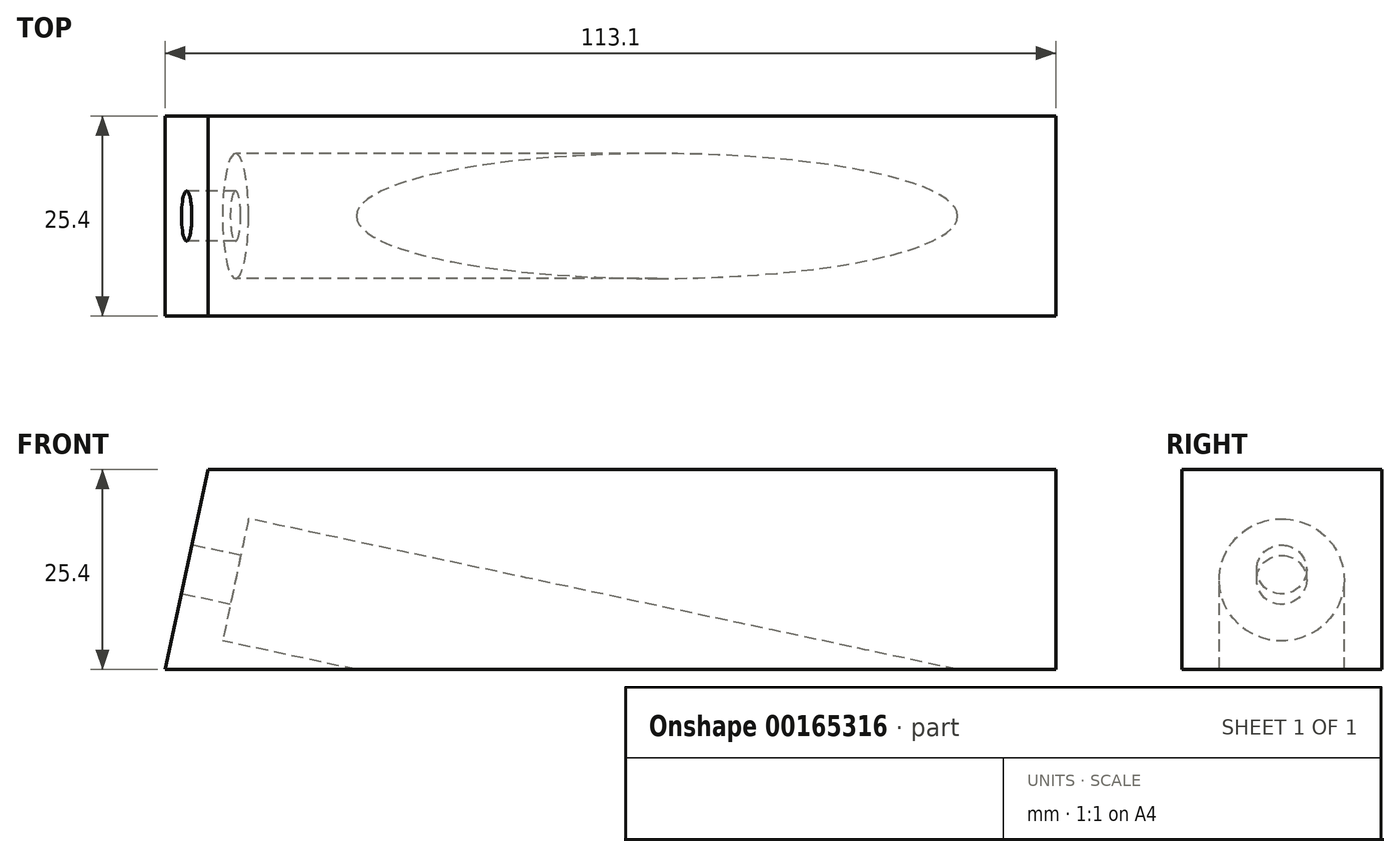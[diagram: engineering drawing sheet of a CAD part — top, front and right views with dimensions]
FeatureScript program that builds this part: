
annotation { "Feature Type Name" : "Feature", "Feature Type Description" : "" }
export const myFeature = defineFeature(function(context is Context, id is Id, definition is map)
    precondition{}
    {
        {
            var Q0;
            Q0=qCreatedBy(makeId("Front.planeOp"),FACE);
            var sketch = newSketch(context, id + "F0", { "sketchPlane" : qUnion([Q0])});
            skLineSegment(sketch, "E0", {"start": v(5.4, 25.4) * mm, "end": v(0, 0) * mm});
            skLineSegment(sketch, "E1", {"start": v(0, 0) * mm, "end": v(113.1, 0) * mm});
            skLineSegment(sketch, "E2", {"start": v(113.1, 0) * mm, "end": v(113.1, 25.4) * mm});
            skLineSegment(sketch, "E3", {"start": v(113.1, 25.4) * mm, "end": v(5.4, 25.4) * mm});
            skSolve(sketch);
        }
        {
            var Q0;
            Q0 = qSketchRegion(id + "F0", true);
            extrude(context, id + "F1", {"entities" : qUnion([Q0]), "endBound" : BoundingType.SYMMETRIC, "depth" : 25.4 * mm});
        }
        {
            var Q0;
            Q0=makeQuery(id+"F1.opExtrude","SWEPT_FACE",FACE,{"disambiguationData":[OSD([sQuery(id+"F0.wireOp",EDGE,"E0")])]});
            var sketch = newSketch(context, id + "F2", { "sketchPlane" : qUnion([Q0])});
            skCircle(sketch, "E4", {"center": v(0, 12.98) * mm, "radius": 3.18 * mm});
            skPoint(sketch, "E4.centerSnap0", {"position": v(12.7, 12.98) * mm});
            skSolve(sketch);
        }
        {
            var Q0;
            Q0 = qSketchRegion(id + "F2", true);
            extrude(context, id + "F3", {"entities" : qUnion([Q0]), "operationType" : NewBodyOperationType.REMOVE, "endBound" : BoundingType.THROUGH_ALL, "oppositeDirection" : true, "depth" : 25.4 * mm});
        }
        {
            var Q0;
            Q0=makeQuery(id+"F1.opExtrude","SWEPT_FACE",FACE,{"disambiguationData":[OSD([sQuery(id+"F0.wireOp",EDGE,"E0")])]});
            cPlane(context, id + "F4", {"entities" : qUnion([Q0]), "cplaneType" : CPlaneType.OFFSET, "offset" : 6.35 * mm, "oppositeDirection" : true, "width" : 152.4 * mm, "height" : 152.4 * mm});
        }
        {
            var Q0;
            Q0=qCreatedBy(id+"F4.planeOp",FACE);
            var sketch = newSketch(context, id + "F5", { "sketchPlane" : qUnion([Q0])});
            skCircle(sketch, "E5.0", {"center": v(0, 12.98) * mm, "radius": 3.18 * mm});
            skCircle(sketch, "E6", {"center": v(0, 12.98) * mm, "radius": 7.94 * mm});
            skSolve(sketch);
        }
        {
            var Q0;
            Q0 = qSketchRegion(id + "F5", true);
            extrude(context, id + "F6", {"entities" : qUnion([Q0]), "operationType" : NewBodyOperationType.REMOVE, "endBound" : BoundingType.THROUGH_ALL, "oppositeDirection" : true, "depth" : 25.4 * mm});
        }
    });
